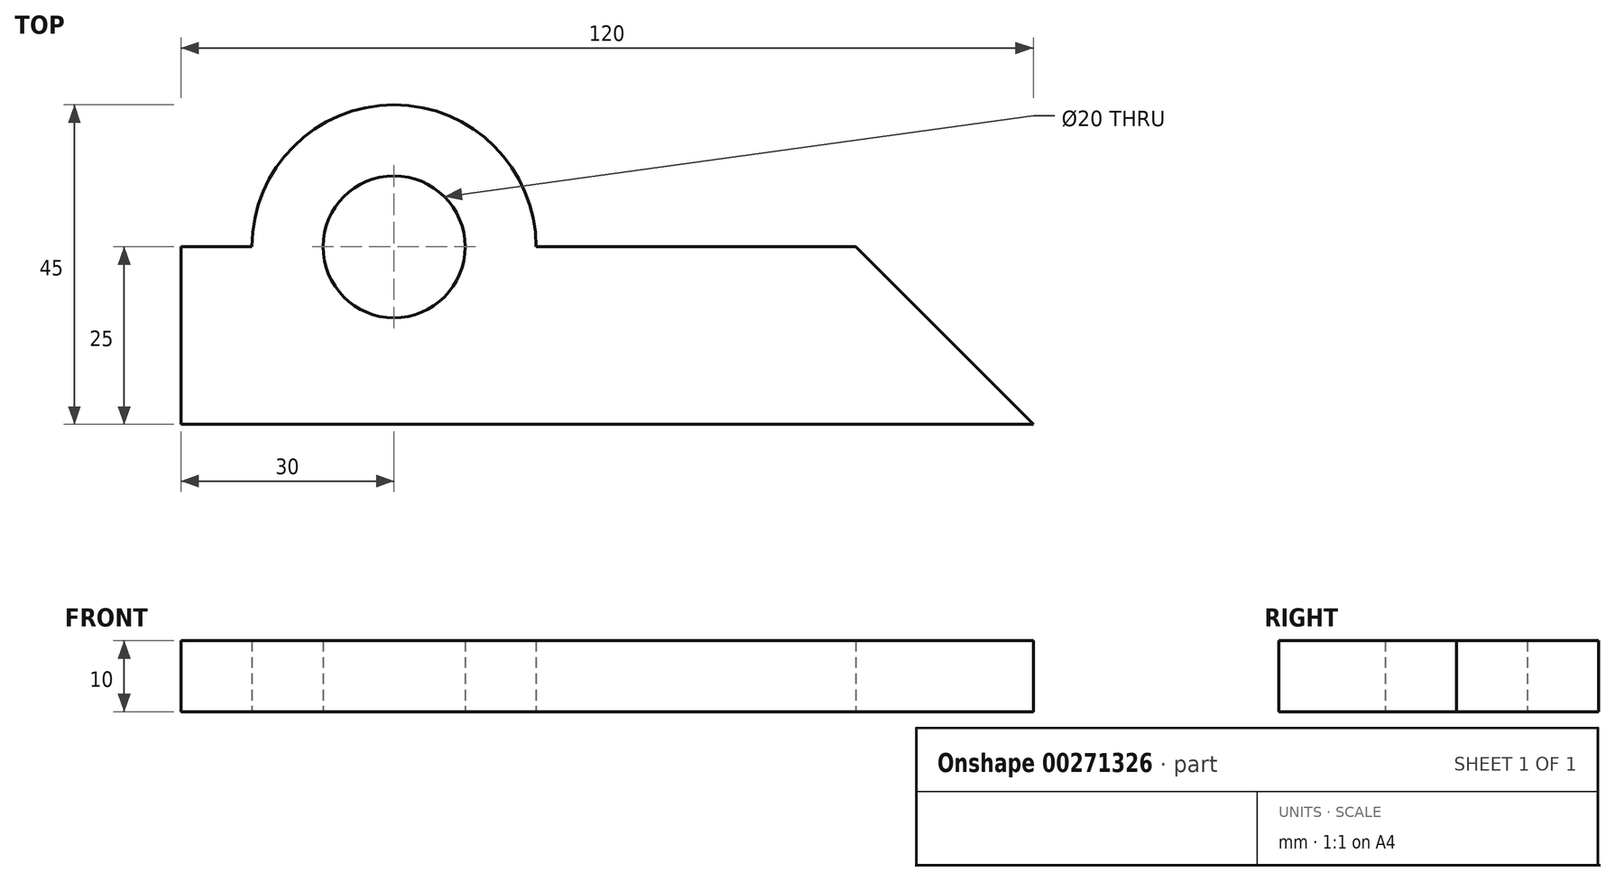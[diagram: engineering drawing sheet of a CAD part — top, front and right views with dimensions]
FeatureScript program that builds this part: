
annotation { "Feature Type Name" : "Feature", "Feature Type Description" : "" }
export const myFeature = defineFeature(function(context is Context, id is Id, definition is map)
    precondition{}
    {
        {
            var Q0;
            Q0=qCreatedBy(makeId("Top.planeOp"),FACE);
            var sketch = newSketch(context, id + "F0", { "sketchPlane" : qUnion([Q0])});
            skLineSegment(sketch, "E0", {"start": v(0, 0) * mm, "end": v(120, 0) * mm});
            skLineSegment(sketch, "E1", {"start": v(0, 0) * mm, "end": v(0, 25) * mm});
            skLineSegment(sketch, "E2", {"start": v(0, 25) * mm, "end": v(10, 25) * mm});
            skArc(sketch, "E3", {"start": v(50, 25) * mm, "mid": v(30, 45) * mm, "end": v(10, 25) * mm});
            skLineSegment(sketch, "E4", {"start": v(50, 25) * mm, "end": v(95, 25) * mm});
            skLineSegment(sketch, "E5", {"start": v(95, 25) * mm, "end": v(120, 0) * mm});
            skCircle(sketch, "E6", {"center": v(30, 25) * mm, "radius": 10 * mm});
            skSolve(sketch);
        }
        {
            var Q0;
            Q0 = qSketchRegion(id + "F0", true);
            extrude(context, id + "F1", {"entities" : qUnion([Q0]), "depth" : 10 * mm});
        }
    });
